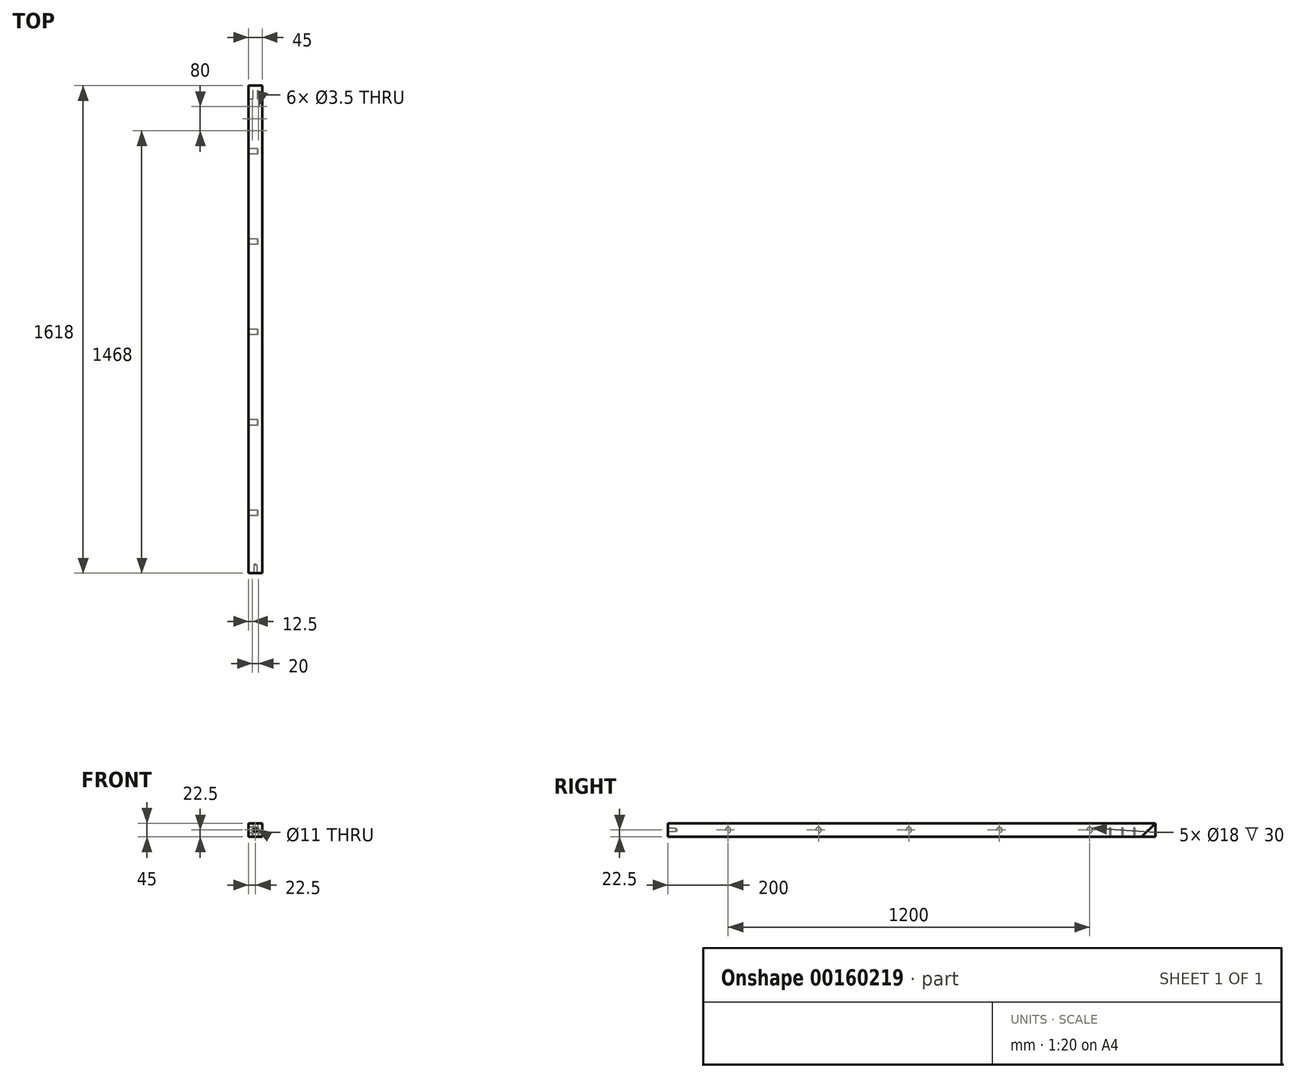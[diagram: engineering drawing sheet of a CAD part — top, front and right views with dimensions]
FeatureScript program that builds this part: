
annotation { "Feature Type Name" : "Feature", "Feature Type Description" : "" }
export const myFeature = defineFeature(function(context is Context, id is Id, definition is map)
    precondition{}
    {
        {
            var Q0;
            Q0=qCreatedBy(makeId("Right.planeOp"),FACE);
            var sketch = newSketch(context, id + "F0", { "sketchPlane" : qUnion([Q0])});
            skLineSegment(sketch, "E0.bottom", {"start": v(0, 22.5) * mm, "end": v(1618, 22.5) * mm});
            skLineSegment(sketch, "E0.top", {"start": v(0, -22.5) * mm, "end": v(1618, -22.5) * mm});
            skLineSegment(sketch, "E0.left", {"start": v(0, 22.5) * mm, "end": v(0, -22.5) * mm});
            skLineSegment(sketch, "E0.right", {"start": v(1618, 22.5) * mm, "end": v(1618, -22.5) * mm});
            skSolve(sketch);
        }
        {
            var Q0;
            Q0=makeQuery(id+"F0.imprint","IMPRINT",FACE,{"disambiguationData":[TD([[makeQuery(id+"F0.imprint","IMPRINT",EDGE,{"derivedFrom":sQuery(id+"F0.wireOp",EDGE,"E0.bottom")}),-1.0]])]});
            extrude(context, id + "F1", {"entities" : qUnion([Q0]), "endBound" : BoundingType.SYMMETRIC, "depth" : 45 * mm});
        }
        {
            var Q0;
            Q0=makeQuery(id+"F1.opExtrude","SWEPT_FACE",FACE,{"disambiguationData":[OSD([sQuery(id+"F0.wireOp",EDGE,"E0.left")])]});
            var sketch = newSketch(context, id + "F2", { "sketchPlane" : qUnion([Q0])});
            skPoint(sketch, "E1", {"position": v(0, 0) * mm});
            skSolve(sketch);
        }
        {
            var Q0;
            Q0=sQuery(id+"F2.wireOp",VERTEX,"E1");
            var Q1;
            Q1=makeQuery(id+"F1.opExtrude","SWEPT_BODY",BODY,{"disambiguationData":[OSD([sQuery(id+"F0.wireOp",EDGE,"E0.bottom"),sQuery(id+"F0.wireOp",EDGE,"E0.top"),sQuery(id+"F0.wireOp",EDGE,"E0.left"),sQuery(id+"F0.wireOp",EDGE,"E0.right")])]});
            hole(context, id + "F3", {"style" : HoleStyle.SIMPLE, "endStyle" : HoleEndStyle.BLIND, "holeDiameter" : 11 * mm, "holeDepth" : 27 * mm, "startFromSketch" : true, "locations" : qUnion([Q0]), "scope" : qUnion([Q1])});
        }
        {
            var Q0;
            Q0=makeQuery(id+"F1.opExtrude","CAP_FACE",FACE,{"disambiguationData":[OSD([sQuery(id+"F0.wireOp",EDGE,"E0.bottom"),sQuery(id+"F0.wireOp",EDGE,"E0.top"),sQuery(id+"F0.wireOp",EDGE,"E0.left"),sQuery(id+"F0.wireOp",EDGE,"E0.right")])],"isStart":false});
            var sketch = newSketch(context, id + "F4", { "sketchPlane" : qUnion([Q0])});
            skLineSegment(sketch, "E2", {"start": v(1618, 22.5) * mm, "end": v(1573, -22.5) * mm});
            skSolve(sketch);
        }
        {
            var Q0;
            {var subQ0=sQuery(id+"F4.wireOp",EDGE,"E2");Q0=makeQuery(id+"F4.imprint","IMPRINT",FACE,{"disambiguationData":[TD([[makeQuery(id+"F4.imprint","IMPRINT",EDGE,{"derivedFrom":subQ0}),1.0]])]});}
            extrude(context, id + "F5", {"entities" : qUnion([Q0]), "operationType" : NewBodyOperationType.REMOVE, "oppositeDirection" : true, "depth" : 15 * mm});
        }
        {
            var Q0;
            Q0=makeQuery(id+"F1.opExtrude","CAP_FACE",FACE,{"disambiguationData":[OSD([sQuery(id+"F0.wireOp",EDGE,"E0.bottom"),sQuery(id+"F0.wireOp",EDGE,"E0.top"),sQuery(id+"F0.wireOp",EDGE,"E0.left"),sQuery(id+"F0.wireOp",EDGE,"E0.right")])],"isStart":true});
            var sketch = newSketch(context, id + "F6", { "sketchPlane" : qUnion([Q0])});
            skLineSegment(sketch, "E3", {"start": v(-1618, 22.5) * mm, "end": v(-1573, -22.5) * mm});
            skSolve(sketch);
        }
        {
            var Q0;
            {var subQ0=sQuery(id+"F6.wireOp",EDGE,"E3");Q0=makeQuery(id+"F6.imprint","IMPRINT",FACE,{"disambiguationData":[TD([[makeQuery(id+"F6.imprint","IMPRINT",EDGE,{"derivedFrom":subQ0}),-1.0]])]});}
            extrude(context, id + "F7", {"entities" : qUnion([Q0]), "operationType" : NewBodyOperationType.REMOVE, "oppositeDirection" : true, "depth" : 15 * mm});
        }
        {
            var Q0;
            Q0=makeQuery(id+"F1.opExtrude","CAP_FACE",FACE,{"disambiguationData":[OSD([sQuery(id+"F0.wireOp",EDGE,"E0.bottom"),sQuery(id+"F0.wireOp",EDGE,"E0.top"),sQuery(id+"F0.wireOp",EDGE,"E0.left"),sQuery(id+"F0.wireOp",EDGE,"E0.right")])],"isStart":true});
            var sketch = newSketch(context, id + "F8", { "sketchPlane" : qUnion([Q0])});
            skCircle(sketch, "E4", {"center": v(-200, 0) * mm, "radius": 9 * mm});
            skCircle(sketch, "E5", {"center": v(-500, 0) * mm, "radius": 9 * mm});
            skCircle(sketch, "E6", {"center": v(-800, 0) * mm, "radius": 9 * mm});
            skCircle(sketch, "E7", {"center": v(-1100, 0) * mm, "radius": 9 * mm});
            skCircle(sketch, "E8", {"center": v(-1400, 0) * mm, "radius": 9 * mm});
            skSolve(sketch);
        }
        {
            var Q0;
            Q0=makeQuery(id+"F8.imprint","IMPRINT",FACE,{"disambiguationData":[TD([[makeQuery(id+"F8.imprint","IMPRINT",EDGE,{"derivedFrom":sQuery(id+"F8.wireOp",EDGE,"E4")}),1.0]])]});
            var Q1;
            Q1=makeQuery(id+"F8.imprint","IMPRINT",FACE,{"disambiguationData":[TD([[makeQuery(id+"F8.imprint","IMPRINT",EDGE,{"derivedFrom":sQuery(id+"F8.wireOp",EDGE,"E5")}),1.0]])]});
            var Q2;
            Q2=makeQuery(id+"F8.imprint","IMPRINT",FACE,{"disambiguationData":[TD([[makeQuery(id+"F8.imprint","IMPRINT",EDGE,{"derivedFrom":sQuery(id+"F8.wireOp",EDGE,"E6")}),1.0]])]});
            var Q3;
            Q3=makeQuery(id+"F8.imprint","IMPRINT",FACE,{"disambiguationData":[TD([[makeQuery(id+"F8.imprint","IMPRINT",EDGE,{"derivedFrom":sQuery(id+"F8.wireOp",EDGE,"E7")}),1.0]])]});
            var Q4;
            Q4=makeQuery(id+"F8.imprint","IMPRINT",FACE,{"disambiguationData":[TD([[makeQuery(id+"F8.imprint","IMPRINT",EDGE,{"derivedFrom":sQuery(id+"F8.wireOp",EDGE,"E8")}),1.0]])]});
            extrude(context, id + "F9", {"entities" : qUnion([Q0, Q1, Q2, Q3, Q4]), "operationType" : NewBodyOperationType.REMOVE, "oppositeDirection" : true, "depth" : 30 * mm});
        }
        {
            var Q0;
            Q0=makeQuery(id+"F1.opExtrude","SWEPT_FACE",FACE,{"disambiguationData":[OSD([sQuery(id+"F0.wireOp",EDGE,"E0.top")])]});
            var sketch = newSketch(context, id + "F10", { "sketchPlane" : qUnion([Q0])});
            skPoint(sketch, "E9", {"position": v(-22.5, 0) * mm});
            skPoint(sketch, "E10", {"position": v(-22.5, -1573) * mm});
            skPoint(sketch, "E11", {"position": v(10, -1548) * mm});
            skPoint(sketch, "E12", {"position": v(10, -1508) * mm});
            skPoint(sketch, "E13", {"position": v(10, -1468) * mm});
            skPoint(sketch, "E14", {"position": v(-10, -1548) * mm});
            skPoint(sketch, "E15", {"position": v(-10, -1508) * mm});
            skPoint(sketch, "E16", {"position": v(-10, -1468) * mm});
            skSolve(sketch);
        }
        {
            var Q0;
            Q0=sQuery(id+"F10.wireOp",VERTEX,"E11");
            var Q1;
            Q1=sQuery(id+"F10.wireOp",VERTEX,"E12");
            var Q2;
            Q2=sQuery(id+"F10.wireOp",VERTEX,"E13");
            var Q3;
            Q3=sQuery(id+"F10.wireOp",VERTEX,"E16");
            var Q4;
            Q4=sQuery(id+"F10.wireOp",VERTEX,"E15");
            var Q5;
            Q5=sQuery(id+"F10.wireOp",VERTEX,"E14");
            var Q6;
            Q6=makeQuery(id+"F1.opExtrude","SWEPT_BODY",BODY,{"disambiguationData":[OSD([sQuery(id+"F0.wireOp",EDGE,"E0.bottom"),sQuery(id+"F0.wireOp",EDGE,"E0.top"),sQuery(id+"F0.wireOp",EDGE,"E0.left"),sQuery(id+"F0.wireOp",EDGE,"E0.right")])]});
            hole(context, id + "F11", {"style" : HoleStyle.SIMPLE, "endStyle" : HoleEndStyle.BLIND, "holeDiameter" : 3.5 * mm, "holeDepth" : 30 * mm, "startFromSketch" : true, "locations" : qUnion([Q0, Q1, Q2, Q3, Q4, Q5]), "scope" : qUnion([Q6])});
        }
    });
